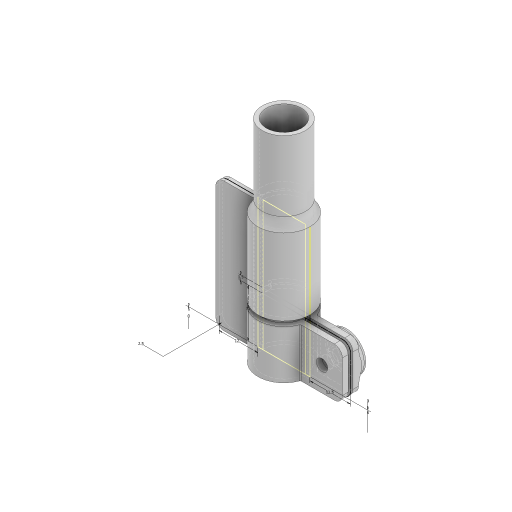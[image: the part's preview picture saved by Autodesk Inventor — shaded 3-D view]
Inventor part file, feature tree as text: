
AUTODESK INVENTOR PART (.ipt)
format: ipt  version: 2023 (Build 270158000, 158)  size: 257,536 bytes
history: native  units: mm
features: extrude x8, sketch x6, fillet x5
ambient origin geometry x8: Origin, YZ Plane, XZ Plane, XY Plane, X Axis, Y Axis, Z Axis, Center Point
bodies: Solid1 (feature_tree)
feature tree (19):
  extrude  "Extrusion1"  Depth=16.0mm
  extrude  "Extrusion2"  Depth=40.0mm TaperAngle=0.0deg
  fillet  "Fillet1"  Radius=13.3mm
  fillet  "Fillet2"  Radius=10.8mm
  sketch  "Sketch3"  dims[d7=25.0mm d8=0.0mm d9=5.0mm]
  extrude  "Extrusion3"  Depth=5.0mm
  extrude  "Extrusion4"  Depth=12.0mm
  extrude  "Extrusion5"  Depth=15.0mm
  extrude  "Extrusion6"  TaperAngle=0.0deg  [1 undecoded]
  fillet  "Fillet3"  Radius=12.5mm
  fillet  "Fillet4"  Radius=2.5mm
  extrude  "Extrusion7"  Depth=2.0mm TaperAngle=0.0deg
  fillet  "Fillet5"  Radius=5.0mm
  extrude  "Extrusion8"  Depth=2.0mm
  sketch  "Sketch1"  dims[d0=13.1mm d1=16.0mm]
  sketch  "Sketch2"  dims[d2=1.45mm d3=40.0mm d4=0.0mm d5=13.3mm d6=10.8mm]
  sketch  "Sketch4"  dims[d10=3.0mm d11=12.0mm]
  sketch  "Sketch5"  dims[d12=0.0mm d13=15.0mm]
  sketch  "Sketch6"  dims[d14=1.5mm d15=0.0mm d16=12.5mm d17=2.5mm d18=2.0mm d19=0.0mm d20=5.0mm d21=0.0mm d22=1.5mm d23=0.75mm d24=15.0mm d25=0.0mm d26=0.0mm d27=0.0mm d28=0.5mm d29=0.5mm d30=12.0mm d31=6.25mm d32=15.0mm d33=7.5mm d34=5.7mm d35=2.5mm d36=0.0mm d37=2.0mm d38=3.5mm d39=0.0mm d40=0.0mm]
note: 1 required parameter value undecoded (feature->parameter linkage not recoverable at this tier; creation-order binding heuristic only, values carry confidence <= 0.55)
